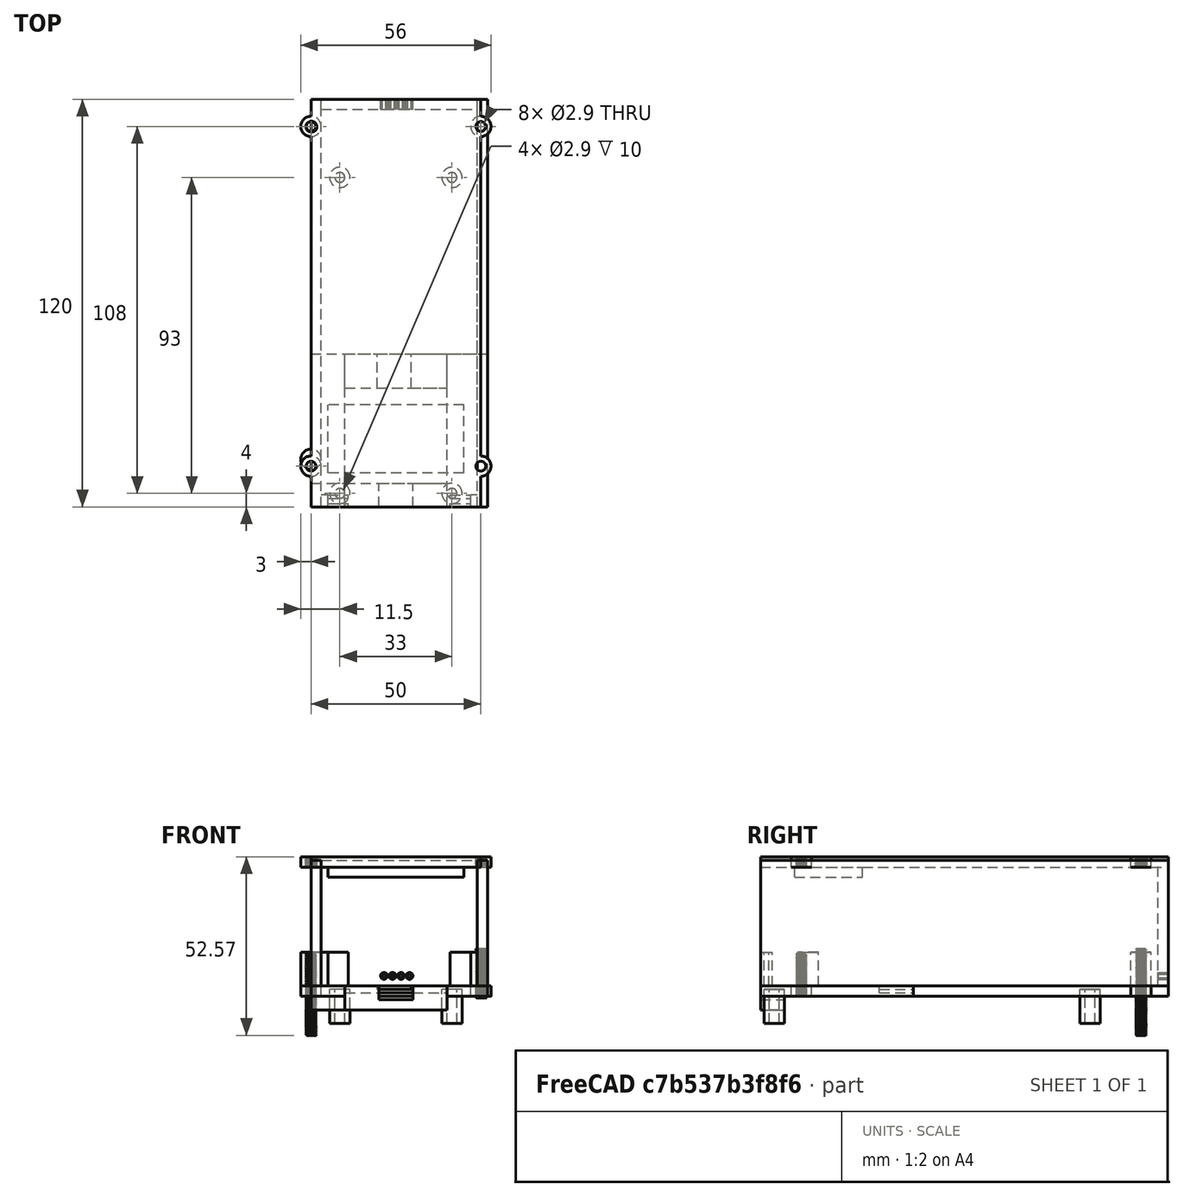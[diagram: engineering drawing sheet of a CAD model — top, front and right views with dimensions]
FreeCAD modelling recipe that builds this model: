
FCSTD DOCUMENT  (FreeCAD 0.19R)
Label: case_rework
License: All rights reserved
LicenseURL: http://en.wikipedia.org/wiki/All_rights_reserved
objects: Part::FeaturePython×62, Part::Cylinder×23, Part::Box×21
note: 106 computed .brp shape members not serialized (recipe doc carries the construction recipe); baked Part::Feature solids carry a one-line shape summary decoded from their .brp

FEATURE [Part::Box] Box007  label="Cube007"
  AttacherType = Attacher::AttachEngine3D
  Height = 3
  Length = 10
  Placement = pos=(-5,0,-2) rot=(0,0,1;0rad)
  Width = 45
FEATURE [Part::Box] Box009  label="Cube009"
  AttacherType = Attacher::AttachEngine3D
  Height = 37
  Length = 46
  Placement = pos=(-2,117,1) rot=(0,0,1;0rad)
  Width = 3
FEATURE [Part::Box] Box016  label="Floor"
  AttacherType = Attacher::AttachEngine3D
  Height = 3
  Length = 50
  Placement = pos=(-5,45,-2) rot=(0,0,1;0rad)
  Width = 75
FEATURE [Part::Box] Box018  label="Cube016"
  AttacherType = Attacher::AttachEngine3D
  Height = 1
  Length = 10
  Placement = pos=(14.5,35,0) rot=(0,0,1;0rad)
  Width = 10
FEATURE [Part::Box] Box008  label="Cube008"
  AttacherType = Attacher::AttachEngine3D
  Height = 2
  Length = 30
  Placement = pos=(5,35,-1) rot=(0,0,1;0rad)
  Width = 10
FEATURE [Part::FeaturePython] Cutout005  # WARN: FeaturePython — macro-defined, semantics opaque (R4)
  Base = -> Box008
  Tolerance = 0
  Tool = -> Box018
FEATURE [Part::Box] Box010  label="Cube010"
  AttacherType = Attacher::AttachEngine3D
  Height = 37
  Length = 3
  Placement = pos=(-5,0,1) rot=(0,0,1;0rad)
  Width = 120
FEATURE [Part::Box] Box020  label="Cube018"
  AttacherType = Attacher::AttachEngine3D
  Height = 3
  Length = 10
  Placement = pos=(45,-1e-14,34) rot=(0,0,1;1.5708rad)
  Width = 50
FEATURE [Part::Box] Box021  label="Cube019"
  AttacherType = Attacher::AttachEngine3D
  Height = 3
  Length = 20
  Placement = pos=(45,10,34) rot=(0,0,1;1.5708rad)
  Width = 50
FEATURE [Part::Box] Box022  label="Cube020"
  AttacherType = Attacher::AttachEngine3D
  Height = 3
  Length = 20
  Placement = pos=(40,10,31) rot=(0,0,1;1.5708rad)
  Width = 40
FEATURE [Part::Box] Box023  label="Cube021"
  AttacherType = Attacher::AttachEngine3D
  Height = 3
  Length = 90
  Placement = pos=(45,30,34) rot=(0,0,1;1.5708rad)
  Width = 50
FEATURE [Part::Box] Box019  label="Cube017"
  AttacherType = Attacher::AttachEngine3D
  Height = 37
  Length = 3
  Placement = pos=(44,0,1) rot=(0,0,1;0rad)
  Width = 120
FEATURE [Part::Box] Box031  label="Cube028"
  AttacherType = Attacher::AttachEngine3D
  Height = 7
  Length = 30
  Placement = pos=(5,0,-6) rot=(0,0,1;0rad)
  Width = 7
FEATURE [Part::Box] Box032  label="Cube029"
  AttacherType = Attacher::AttachEngine3D
  Height = 4
  Length = 10
  Placement = pos=(15,0,-3) rot=(0,0,1;0rad)
  Width = 7
FEATURE [Part::Cylinder] Cylinder036  label="outer016"
  Angle = 360
  AttacherType = Attacher::AttachEngine3D
  Height = 3
  Placement = pos=(-69,17,-9) rot=(0,0,1;0rad)
  Radius = 3
FEATURE [Part::Cylinder] Cylinder038  label="M3 cutout021"
  Angle = 360
  AttacherType = Attacher::AttachEngine3D
  Height = 3
  Placement = pos=(-69,17,-9) rot=(0,0,1;0rad)
  Radius = 1.45
FEATURE [Part::FeaturePython] Cutout007  # WARN: FeaturePython — macro-defined, semantics opaque (R4)
  Base = -> Cylinder036
  Placement = pos=(64,95,7) rot=(0,0,1;0rad)
  Tolerance = 0
  Tool = -> Cylinder038
FEATURE [Part::Cylinder] Cylinder051  label="M3 cutout029"
  Angle = 360
  AttacherType = Attacher::AttachEngine3D
  Height = 10
  Placement = pos=(5,94,-10) rot=(0,0,1;0rad)
  Radius = 1.45
FEATURE [Part::Cylinder] Cylinder052  label="outer023"
  Angle = 360
  AttacherType = Attacher::AttachEngine3D
  Height = 10
  Placement = pos=(5,94,-10) rot=(0,0,1;0rad)
  Radius = 3
FEATURE [Part::Cylinder] Cylinder053  label="M3 cutout030"
  Angle = 360
  AttacherType = Attacher::AttachEngine3D
  Height = 10
  Placement = pos=(5,94,-10) rot=(0,0,1;0rad)
  Radius = 1.45
FEATURE [Part::Cylinder] Cylinder054  label="outer024"
  Angle = 360
  AttacherType = Attacher::AttachEngine3D
  Height = 10
  Placement = pos=(5,94,-10) rot=(0,0,1;0rad)
  Radius = 3
FEATURE [Part::FeaturePython] Cutout013  label="Batter holder screw 2"  # WARN: FeaturePython — macro-defined, semantics opaque (R4)
  Base = -> Cylinder054
  Placement = pos=(31.5,3,0) rot=(0,0,1;0rad)
  Tolerance = 0
  Tool = -> Cylinder053
FEATURE [Part::Cylinder] Cylinder055  label="M3 cutout031"
  Angle = 360
  AttacherType = Attacher::AttachEngine3D
  Height = 10
  Placement = pos=(5,94,-10) rot=(0,0,1;0rad)
  Radius = 1.45
FEATURE [Part::Cylinder] Cylinder056  label="outer025"
  Angle = 360
  AttacherType = Attacher::AttachEngine3D
  Height = 10
  Placement = pos=(5,94,-10) rot=(0,0,1;0rad)
  Radius = 3
FEATURE [Part::FeaturePython] Cutout014  label="Batter holder screw 3"  # WARN: FeaturePython — macro-defined, semantics opaque (R4)
  Base = -> Cylinder056
  Placement = pos=(31.5,-90,0) rot=(0,0,1;0rad)
  Tolerance = 0
  Tool = -> Cylinder055
FEATURE [Part::Cylinder] Cylinder058  label="outer026"
  Angle = 360
  AttacherType = Attacher::AttachEngine3D
  Height = 10
  Placement = pos=(5,94,-10) rot=(0,0,1;0rad)
  Radius = 3
FEATURE [Part::Cylinder] Cylinder059  label="M3 cutout033"
  Angle = 360
  AttacherType = Attacher::AttachEngine3D
  Height = 10
  Placement = pos=(5,94,-10) rot=(0,0,1;0rad)
  Radius = 1.45
FEATURE [Part::FeaturePython] Cutout018  label="Batter holder screw 004"  # WARN: FeaturePython — macro-defined, semantics opaque (R4)
  Base = -> Cylinder058
  Placement = pos=(-1.5,-90,0) rot=(0,0,1;0rad)
  Tolerance = 0
  Tool = -> Cylinder059
FEATURE [Part::Box] Box006  label="Cube006"
  AttacherType = Attacher::AttachEngine3D
  Height = 3
  Length = 12
  Placement = pos=(35,0,-2) rot=(0,0,1;0rad)
  Width = 45
FEATURE [Part::FeaturePython] Cutout  # WARN: FeaturePython — macro-defined, semantics opaque (R4)
  Base = -> Box031
  Tolerance = 0
  Tool = -> Box032
FEATURE [Part::FeaturePython] Cutout015  # WARN: FeaturePython — macro-defined, semantics opaque (R4)
  Base = -> Cutout
  Tolerance = 0
  Tool = -> Cylinder055
FEATURE [Part::Box] Box033  label="Cube030"
  AttacherType = Attacher::AttachEngine3D
  Height = 4
  Length = 10
  Placement = pos=(-5,0,-6) rot=(0,0,1;0rad)
  Width = 7
FEATURE [Part::Cylinder] Cylinder074  label="M3 cutout044"
  Angle = 360
  AttacherType = Attacher::AttachEngine3D
  Height = 10
  Placement = pos=(3.5,4,-10) rot=(0,0,1;0rad)
  Radius = 1.45
FEATURE [Part::FeaturePython] Cutout031  # WARN: FeaturePython — macro-defined, semantics opaque (R4)
  Base = -> Box033
  Tolerance = 0
  Tool = -> Cylinder074
FEATURE [Part::FeaturePython] Cutout032  # WARN: FeaturePython — macro-defined, semantics opaque (R4)
  Base = -> Box033
  Placement = pos=(40,1e-15,-8) rot=(0,1,0;3.14159rad)
  Tolerance = 0
  Tool = -> Cylinder074
FEATURE [Part::FeaturePython] Connect006  # WARN: FeaturePython — macro-defined, semantics opaque (R4)
  Placement = pos=(0,-100,0) rot=(0,0,1;0rad)
  Tolerance = 0
FEATURE [Part::FeaturePython] Connect007  # WARN: FeaturePython — macro-defined, semantics opaque (R4)
  Placement = pos=(50,0,0) rot=(0,0,1;0rad)
  Tolerance = 0
FEATURE [Part::FeaturePython] Connect011  # WARN: FeaturePython — macro-defined, semantics opaque (R4)
  Placement = pos=(50,224,37) rot=(1,0,0;3.14159rad)
  Tolerance = 0
FEATURE [Part::FeaturePython] Connect013  # WARN: FeaturePython — macro-defined, semantics opaque (R4)
  Placement = pos=(0,124,37) rot=(1,0,0;3.14159rad)
  Tolerance = 0
FEATURE [Part::Cylinder] Cylinder083  label="M3 cutout053"
  Angle = 360
  AttacherType = Attacher::AttachEngine3D
  Height = 3
  Placement = pos=(-5,12,34) rot=(0,0,1;0rad)
  Radius = 1.45
FEATURE [Part::FeaturePython] Cutout039  # WARN: FeaturePython — macro-defined, semantics opaque (R4)
  Base = -> Box021
  Tolerance = 0
  Tool = -> Cylinder083
FEATURE [Part::Cylinder] Cylinder084  label="M3 cutout054"
  Angle = 360
  AttacherType = Attacher::AttachEngine3D
  Height = 3
  Placement = pos=(45,12,34) rot=(0,0,1;0rad)
  Radius = 1.45
FEATURE [Part::FeaturePython] Cutout041  # WARN: FeaturePython — macro-defined, semantics opaque (R4)
  Base = -> Cutout039
  Tolerance = 0
  Tool = -> Cylinder084
FEATURE [Part::Cylinder] Cylinder085  label="M3 cutout055"
  Angle = 360
  AttacherType = Attacher::AttachEngine3D
  Height = 3
  Placement = pos=(45,112,34) rot=(0,0,1;0rad)
  Radius = 1.45
FEATURE [Part::FeaturePython] Cutout043  # WARN: FeaturePython — macro-defined, semantics opaque (R4)
  Base = -> Box023
  Tolerance = 0
  Tool = -> Cylinder085
FEATURE [Part::Cylinder] Cylinder086  label="M3 cutout056"
  Angle = 360
  AttacherType = Attacher::AttachEngine3D
  Height = 3
  Placement = pos=(-5,112,34) rot=(0,0,1;0rad)
  Radius = 1.45
FEATURE [Part::FeaturePython] Cutout045  # WARN: FeaturePython — macro-defined, semantics opaque (R4)
  Base = -> Cutout043
  Tolerance = 0
  Tool = -> Cylinder086
FEATURE [Part::FeaturePython] ScrewTap001  label="M3x10.0-ScrewTap006"  # Fasteners workbench fastener (typed FeaturePython)
  Placement = pos=(36.5,4,-10) rot=(0,0,1;0rad)
  baseObject = -> Cutout014 [Edge5]
  diameter = 4
  diameterCustom = 6
  invert = false
  length = 10
  matchOuter = false
  offset = 0
  pitchCustom = 1
  thread = true
FEATURE [Part::FeaturePython] ScrewTap002  label="M3x10.0-ScrewTap"  # Fasteners workbench fastener (typed FeaturePython)
  Placement = pos=(3.5,4,-10) rot=(0,0,1;0rad)
  baseObject = -> Cutout018 [Edge5]
  diameter = 4
  diameterCustom = 6
  invert = false
  length = 10
  matchOuter = false
  offset = 0
  pitchCustom = 1
  thread = true
FEATURE [Part::FeaturePython] Cutout056  # WARN: FeaturePython — macro-defined, semantics opaque (R4)
  Base = -> Cutout032
  Tolerance = 0
  Tool = -> ScrewTap001
FEATURE [Part::FeaturePython] Cutout057  # WARN: FeaturePython — macro-defined, semantics opaque (R4)
  Base = -> Cutout014
  Tolerance = 0
  Tool = -> ScrewTap001
FEATURE [Part::FeaturePython] Cutout058  # WARN: FeaturePython — macro-defined, semantics opaque (R4)
  Base = -> Cutout015
  Tolerance = 0
FEATURE [Part::FeaturePython] Cutout060  # WARN: FeaturePython — macro-defined, semantics opaque (R4)
  Base = -> Cutout058
  Tolerance = 0
  Tool = -> ScrewTap002
FEATURE [Part::FeaturePython] Cutout062  # WARN: FeaturePython — macro-defined, semantics opaque (R4)
  Base = -> Cutout031
  Tolerance = 0
  Tool = -> ScrewTap002
FEATURE [Part::Cylinder] Cylinder088  label="M3 cutout058"
  Angle = 360
  AttacherType = Attacher::AttachEngine3D
  Height = 3
  Placement = pos=(-69,17,-9) rot=(0,0,1;0rad)
  Radius = 1.45
FEATURE [Part::Cylinder] Cylinder089  label="outer028"
  Angle = 360
  AttacherType = Attacher::AttachEngine3D
  Height = 3
  Placement = pos=(-69,17,-9) rot=(0,0,1;0rad)
  Radius = 3
FEATURE [Part::FeaturePython] Cutout087  # WARN: FeaturePython — macro-defined, semantics opaque (R4)
  Base = -> Cutout018
  Tolerance = 0
  Tool = -> ScrewTap002
FEATURE [Part::FeaturePython] Cutout088  # WARN: FeaturePython — macro-defined, semantics opaque (R4)
  Base = -> Cutout013
  Tolerance = 0
FEATURE [Part::FeaturePython] ScrewTap018  label="M3x10.0-ScrewTap022"  # Fasteners workbench fastener (typed FeaturePython)
  Placement = pos=(36.5,4,-10) rot=(0,0,1;0rad)
  baseObject = -> Cutout057 [Edge5]
  diameter = 4
  diameterCustom = 6
  invert = false
  length = 10
  matchOuter = false
  offset = 0
  pitchCustom = 1
  thread = true
FEATURE [Part::FeaturePython] Cutout092  # WARN: FeaturePython — macro-defined, semantics opaque (R4)
  Base = -> Cutout057
  Tolerance = 0
  Tool = -> ScrewTap018
FEATURE [Part::FeaturePython] ScrewTap021  label="M3x10.0-ScrewTap025"  # Fasteners workbench fastener (typed FeaturePython)
  Placement = pos=(36.5,97,-10) rot=(0,0,1;0rad)
  baseObject = -> Cutout088 [Edge5]
  diameter = 4
  diameterCustom = 6
  invert = false
  length = 10
  matchOuter = false
  offset = 0
  pitchCustom = 1
  thread = true
FEATURE [Part::FeaturePython] Cutout093  # WARN: FeaturePython — macro-defined, semantics opaque (R4)
  Base = -> Cutout088
  Tolerance = 0
  Tool = -> ScrewTap021
FEATURE [Part::FeaturePython] Cutout094  # WARN: FeaturePython — macro-defined, semantics opaque (R4)
  Base = -> Cutout092
  Tolerance = 0
  Tool = -> ScrewTap018
FEATURE [Part::Box] Box  label="Cube"
  AttacherType = Attacher::AttachEngine3D
  Height = 10
  Length = 6
  Placement = pos=(0,0,1) rot=(0,0,1;0rad)
  Width = 1
FEATURE [Part::Box] Box001  label="Cube001"
  AttacherType = Attacher::AttachEngine3D
  Height = 10
  Length = 3.5
  Placement = pos=(-2e-16,0,1) rot=(0,0,1;1.5708rad)
  Width = 2
FEATURE [Part::Box] Box002  label="Cube002"
  AttacherType = Attacher::AttachEngine3D
  Height = 10
  Length = 6
  Placement = pos=(0,2.5,1) rot=(0,0,1;0rad)
  Width = 1
FEATURE [Part::Box] Box034  label="Cube031"
  AttacherType = Attacher::AttachEngine3D
  Height = 10
  Length = 3.5
  Placement = pos=(44,-9e-15,1) rot=(0,0,1;1.5708rad)
  Width = 2
FEATURE [Part::Box] Box035  label="Cube032"
  AttacherType = Attacher::AttachEngine3D
  Height = 10
  Length = 6
  Placement = pos=(36,0,1) rot=(0,0,1;0rad)
  Width = 1
FEATURE [Part::Box] Box036  label="Cube033"
  AttacherType = Attacher::AttachEngine3D
  Height = 10
  Length = 6
  Placement = pos=(36,2.5,1) rot=(0,0,1;0rad)
  Width = 1
FEATURE [Part::FeaturePython] Tube  # WARN: FeaturePython — macro-defined, semantics opaque (R4)
  AttacherType = Attacher::AttachEngine3D
  Height = 3
  InnerRadius = 0.5
  OuterRadius = 1
  Placement = pos=(16.5,117,4) rot=(0,0.707107,0.707107;3.14159rad)
FEATURE [Part::FeaturePython] Tube001  # WARN: FeaturePython — macro-defined, semantics opaque (R4)
  AttacherType = Attacher::AttachEngine3D
  Height = 3
  InnerRadius = 0.5
  OuterRadius = 1
  Placement = pos=(19,117,4) rot=(-1,0,0;1.5708rad)
FEATURE [Part::FeaturePython] Tube002  # WARN: FeaturePython — macro-defined, semantics opaque (R4)
  AttacherType = Attacher::AttachEngine3D
  Height = 3
  InnerRadius = 0.5
  OuterRadius = 1
  Placement = pos=(21.5,117,4) rot=(-1,0,0;1.5708rad)
FEATURE [Part::FeaturePython] Tube003  # WARN: FeaturePython — macro-defined, semantics opaque (R4)
  AttacherType = Attacher::AttachEngine3D
  Height = 3
  InnerRadius = 0.5
  OuterRadius = 1
  Placement = pos=(24,117,4) rot=(-1,0,0;1.5708rad)
FEATURE [Part::FeaturePython] Cutout012  label="Batter holder screw 1"  # WARN: FeaturePython — macro-defined, semantics opaque (R4)
  Base = -> Cylinder052
  Placement = pos=(-1.5,3,0) rot=(0,0,1;0rad)
  Tolerance = 0
  Tool = -> Cylinder051
FEATURE [Part::FeaturePython] Cutout090  # WARN: FeaturePython — macro-defined, semantics opaque (R4)
  Base = -> Cutout012
  Tolerance = 0
FEATURE [Part::Cylinder] Cylinder090  label="M3Outer"
  Angle = 360
  AttacherType = Attacher::AttachEngine3D
  Height = 10
  Placement = pos=(-5,112,1) rot=(0,0,1;0rad)
  Radius = 3
FEATURE [Part::FeaturePython] ScrewTap022  label="M3x9.0-ScrewTap"  # Fasteners workbench fastener (typed FeaturePython)
  Placement = pos=(-5,112,1) rot=(0,0,1;0rad)
  baseObject = -> Cylinder090 [Edge3]
  diameter = 4
  diameterCustom = 6
  invert = false
  length = 9
  matchOuter = false
  offset = 0
  pitchCustom = 1
  thread = true
FEATURE [Part::FeaturePython] Cutout103  # WARN: FeaturePython — macro-defined, semantics opaque (R4)
  Base = -> Cylinder090
  Tolerance = 0
  Tool = -> ScrewTap022
FEATURE [Part::Cylinder] Cylinder091  label="M3Outer001"
  Angle = 360
  AttacherType = Attacher::AttachEngine3D
  Height = 10
  Placement = pos=(-5,112,1) rot=(0,0,1;0rad)
  Radius = 3
FEATURE [Part::FeaturePython] ScrewTap023  label="M3x9.0-ScrewTap003"  # Fasteners workbench fastener (typed FeaturePython)
  Placement = pos=(-5,112,1) rot=(0,0,1;0rad)
  baseObject = -> Cylinder091 [Edge3]
  diameter = 4
  diameterCustom = 6
  invert = false
  length = 9
  matchOuter = false
  offset = 0
  pitchCustom = 1
  thread = true
FEATURE [Part::FeaturePython] Cutout104  # WARN: FeaturePython — macro-defined, semantics opaque (R4)
  Base = -> Cylinder091
  Placement = pos=(0,-98,0) rot=(0,0,1;0rad)
  Tolerance = 0
  Tool = -> ScrewTap023
FEATURE [Part::Cylinder] Cylinder092  label="M3Outer002"
  Angle = 360
  AttacherType = Attacher::AttachEngine3D
  Height = 10
  Placement = pos=(-5,112,1) rot=(0,0,1;0rad)
  Radius = 3
FEATURE [Part::FeaturePython] ScrewTap024  label="M3x9.0-ScrewTap004"  # Fasteners workbench fastener (typed FeaturePython)
  Placement = pos=(-5,112,1) rot=(0,0,1;0rad)
  baseObject = -> Cylinder092 [Edge3]
  diameter = 4
  diameterCustom = 6
  invert = false
  length = 9
  matchOuter = false
  offset = 0
  pitchCustom = 1
  thread = true
FEATURE [Part::FeaturePython] Cutout105  # WARN: FeaturePython — macro-defined, semantics opaque (R4)
  Base = -> Cylinder092
  Tolerance = 0
  Tool = -> ScrewTap024
FEATURE [Part::FeaturePython] Cutout025  # WARN: FeaturePython — macro-defined, semantics opaque (R4)
  Base = -> Box007
  Tolerance = 0
FEATURE [Part::FeaturePython] Cutout011  # WARN: FeaturePython — macro-defined, semantics opaque (R4)
  Placement = pos=(114,95,7) rot=(0,0,1;0rad)
  Tolerance = 0
FEATURE [Part::FeaturePython] Cutout086  # WARN: FeaturePython — macro-defined, semantics opaque (R4)
  Base = -> Cylinder089
  Placement = pos=(64,-5,7) rot=(0,0,1;0rad)
  Tolerance = 0
  Tool = -> Cylinder088
FEATURE [Part::FeaturePython] Cutout052  # WARN: FeaturePython — macro-defined, semantics opaque (R4)
  Base = -> Cutout007
  Tolerance = 0
FEATURE [Part::Cylinder] Cylinder064  label="outer027"
  Angle = 360
  AttacherType = Attacher::AttachEngine3D
  Height = 3
  Placement = pos=(-69,17,-9) rot=(0,0,1;0rad)
  Radius = 3
FEATURE [Part::Cylinder] Cylinder065  label="M3 cutout038"
  Angle = 360
  AttacherType = Attacher::AttachEngine3D
  Height = 3
  Placement = pos=(-69,17,-9) rot=(0,0,1;0rad)
  Radius = 1.45
FEATURE [Part::FeaturePython] Cutout038  # WARN: FeaturePython — macro-defined, semantics opaque (R4)
  Base = -> Cylinder064
  Placement = pos=(64,-5,43) rot=(0,0,1;0rad)
  Tolerance = 0
  Tool = -> Cylinder065
FEATURE [Part::FeaturePython] Cutout040  # WARN: FeaturePython — macro-defined, semantics opaque (R4)
  Base = -> Cylinder064
  Placement = pos=(114,-5,43) rot=(0,0,1;0rad)
  Tolerance = 0
  Tool = -> Cylinder065
FEATURE [Part::FeaturePython] Cutout042  # WARN: FeaturePython — macro-defined, semantics opaque (R4)
  Base = -> Cylinder064
  Placement = pos=(114,95,43) rot=(0,0,1;0rad)
  Tolerance = 0
  Tool = -> Cylinder065
FEATURE [Part::FeaturePython] Cutout044  # WARN: FeaturePython — macro-defined, semantics opaque (R4)
  Base = -> Cylinder064
  Placement = pos=(64,95,43) rot=(0,0,1;0rad)
  Tolerance = 0
  Tool = -> Cylinder065
FEATURE [Part::FeaturePython] Connect016  label="lid"  # WARN: FeaturePython — macro-defined, semantics opaque (R4)
  Objects = -> [Box020,Box022,Cutout040,Cutout041,Cutout045,Cutout044,Cutout042,Cutout038]
  Placement = pos=(0,0,2) rot=(0,0,1;0rad)
  Tolerance = 0
FEATURE [Part::FeaturePython] Cutout068  # WARN: FeaturePython — macro-defined, semantics opaque (R4)
  Base = -> Connect016
  Tolerance = 0
FEATURE [Part::FeaturePython] Cutout070  # WARN: FeaturePython — macro-defined, semantics opaque (R4)
  Base = -> Cutout068
  Tolerance = 0
FEATURE [Part::FeaturePython] Cutout072  # WARN: FeaturePython — macro-defined, semantics opaque (R4)
  Base = -> Cutout070
  Tolerance = 0
FEATURE [Part::FeaturePython] Cutout074  # WARN: FeaturePython — macro-defined, semantics opaque (R4)
  Base = -> Cutout072
  Tolerance = 0
FEATURE [Part::FeaturePython] Cutout076  # WARN: FeaturePython — macro-defined, semantics opaque (R4)
  Base = -> Cutout074
  Tolerance = 0
FEATURE [Part::FeaturePython] Cutout102  # WARN: FeaturePython — macro-defined, semantics opaque (R4)
  Base = -> Cutout076
  Tolerance = 0
FEATURE [Part::FeaturePython] Cutout024  # WARN: FeaturePython — macro-defined, semantics opaque (R4)
  Base = -> Cylinder064
  Placement = pos=(64,-5,7) rot=(0,0,1;0rad)
  Tolerance = 0
  Tool = -> Cylinder065
FEATURE [Part::FeaturePython] ScrewTap016  label="M3x12.0-ScrewTap018"  # Fasteners workbench fastener (typed FeaturePython)
  Placement = pos=(-5,12,10.5) rot=(0,0,1;0rad)
  diameter = 4
  diameterCustom = 6
  invert = false
  length = 12
  matchOuter = false
  offset = 0
  pitchCustom = 1
  thread = true
FEATURE [Part::Cylinder] Cylinder093  label="M3Outer003"
  Angle = 360
  AttacherType = Attacher::AttachEngine3D
  Height = 10
  Placement = pos=(-5,112,1) rot=(0,0,1;0rad)
  Radius = 3
FEATURE [Part::FeaturePython] ScrewTap025  label="M3x14.0-ScrewTap"  # Fasteners workbench fastener (typed FeaturePython)
  Placement = pos=(-5,112,1) rot=(0,0,1;0rad)
  baseObject = -> Cylinder093 [Edge3]
  diameter = 4
  diameterCustom = 6
  invert = false
  length = 14
  matchOuter = false
  offset = 0
  pitchCustom = 1
  thread = true
FEATURE [Part::FeaturePython] ScrewTap026  label="M3x14.0-ScrewTap001"  # Fasteners workbench fastener (typed FeaturePython)
  Placement = pos=(45,112,12) rot=(0,0,1;0rad)
  baseObject = -> Cylinder093 [Edge3]
  diameter = 4
  diameterCustom = 6
  invert = false
  length = 14
  matchOuter = false
  offset = 0
  pitchCustom = 1
  thread = true
